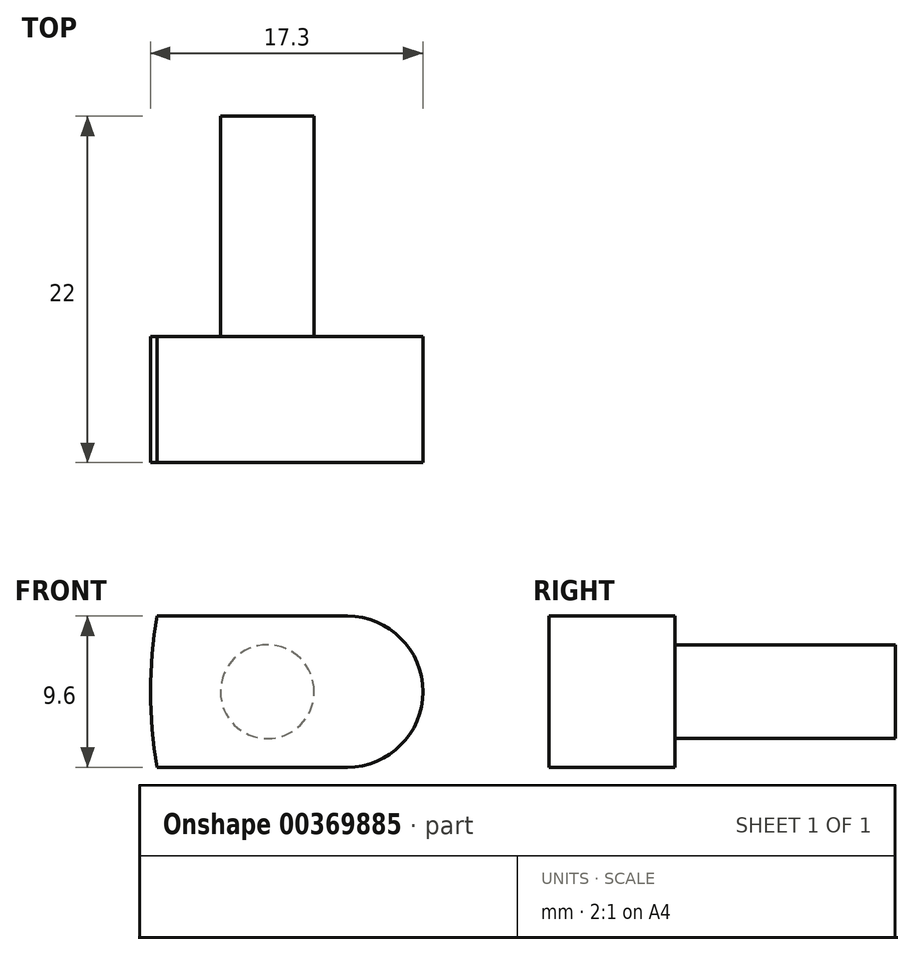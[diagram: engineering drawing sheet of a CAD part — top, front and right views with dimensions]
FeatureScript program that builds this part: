
annotation { "Feature Type Name" : "Feature", "Feature Type Description" : "" }
export const myFeature = defineFeature(function(context is Context, id is Id, definition is map)
    precondition{}
    {
        {
            var Q0;
            Q0=qCreatedBy(makeId("Front.planeOp"),FACE);
            var sketch = newSketch(context, id + "F0", { "sketchPlane" : qUnion([Q0])});
            skArc(sketch, "E0", {"start": v(-27.08, 4.8) * mm, "mid": v(-27.5, 0) * mm, "end": v(-27.08, -4.8) * mm});
            skLineSegment(sketch, "E1.bottom", {"start": v(-27.08, 4.8) * mm, "end": v(-15, 4.8) * mm});
            skLineSegment(sketch, "E1.top", {"start": v(-27.08, -4.8) * mm, "end": v(-15, -4.8) * mm});
            skArc(sketch, "E2", {"start": v(-15, -4.8) * mm, "mid": v(-10.2, 0) * mm, "end": v(-15, 4.8) * mm});
            skSolve(sketch);
        }
        {
            var Q0;
            Q0=makeQuery(id+"F0.imprint","IMPRINT",FACE,{"disambiguationData":[TD([[makeQuery(id+"F0.imprint","IMPRINT",EDGE,{"derivedFrom":sQuery(id+"F0.wireOp",EDGE,"E0")}),1.0]])]});
            extrude(context, id + "F1", {"entities" : qUnion([Q0]), "depth" : 8 * mm});
        }
        {
            var Q0;
            Q0=makeQuery(id+"F1.opExtrude","CAP_FACE",FACE,{"disambiguationData":[OSD([sQuery(id+"F0.wireOp",EDGE,"E0"),sQuery(id+"F0.wireOp",EDGE,"E1.bottom"),sQuery(id+"F0.wireOp",EDGE,"E1.top"),sQuery(id+"F0.wireOp",EDGE,"E2")])],"isStart":true});
            var sketch = newSketch(context, id + "F2", { "sketchPlane" : qUnion([Q0])});
            skLineSegment(sketch, "E3", {"start": v(20.08, 11.64) * mm, "end": v(20.08, -15.4) * mm, "construction": true});
            skLineSegment(sketch, "E4", {"start": v(6.78, 0) * mm, "end": v(28.75, 0) * mm, "construction": true});
            skCircle(sketch, "E5", {"center": v(20.08, 0) * mm, "radius": 2.98 * mm});
            skSolve(sketch);
        }
        {
            var Q0;
            Q0=makeQuery(id+"F2.imprint","IMPRINT",FACE,{"disambiguationData":[TD([[makeQuery(id+"F2.imprint","IMPRINT",EDGE,{"derivedFrom":sQuery(id+"F2.wireOp",EDGE,"E5")}),1.0]])]});
            extrude(context, id + "F3", {"entities" : qUnion([Q0]), "operationType" : NewBodyOperationType.ADD, "depth" : 14 * mm});
        }
    });
